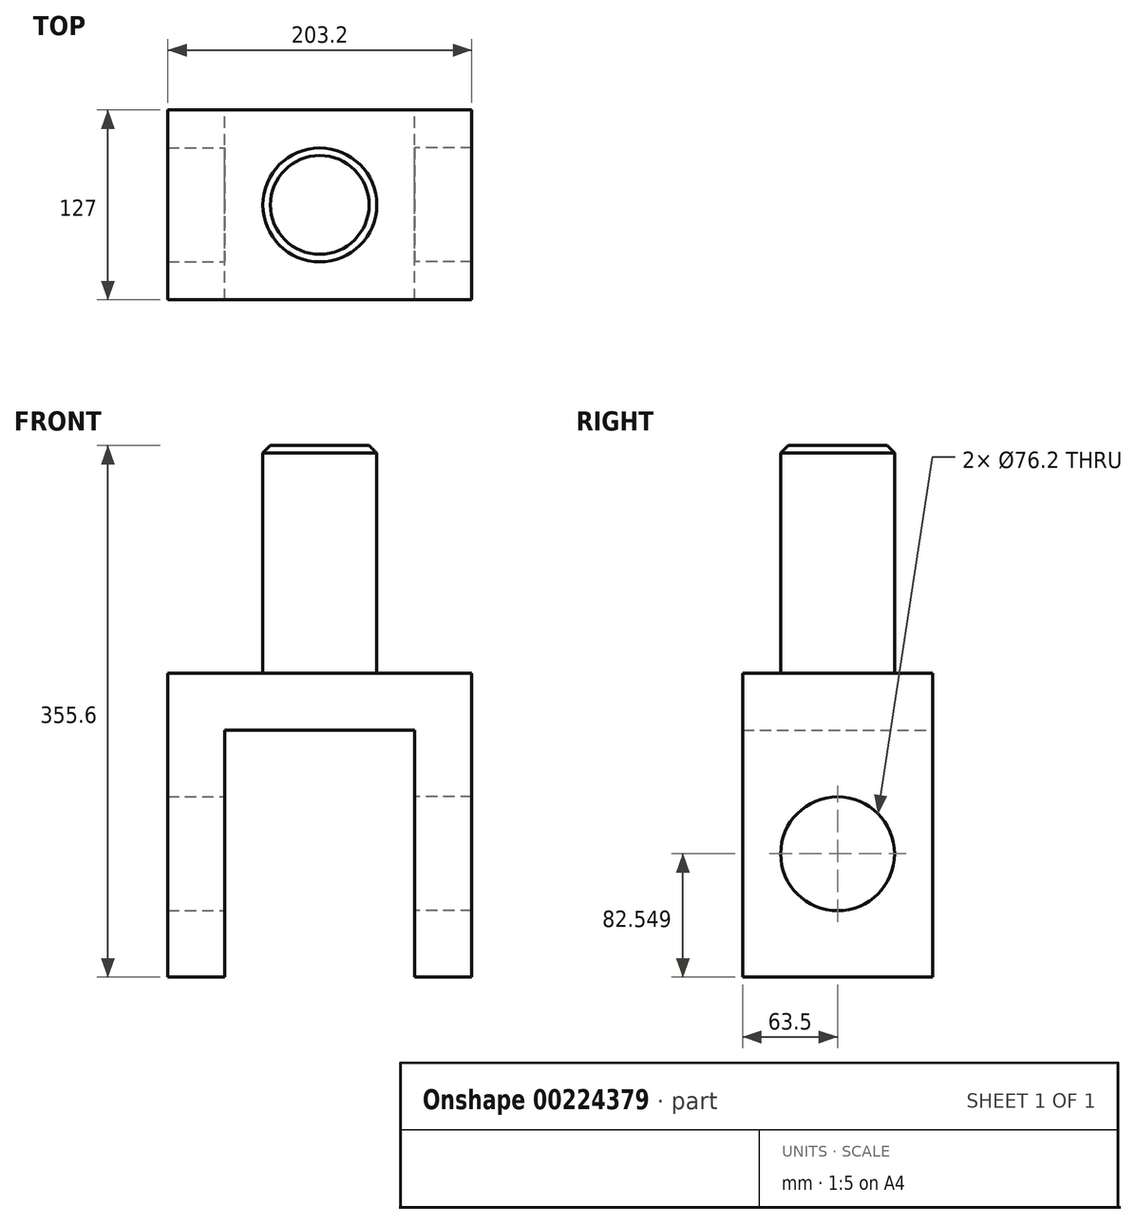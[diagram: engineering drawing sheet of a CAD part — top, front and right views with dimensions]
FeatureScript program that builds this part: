
annotation { "Feature Type Name" : "Feature", "Feature Type Description" : "" }
export const myFeature = defineFeature(function(context is Context, id is Id, definition is map)
    precondition{}
    {
        {
            var Q0;
            Q0=qCreatedBy(makeId("Front.planeOp"),FACE);
            var sketch = newSketch(context, id + "F0", { "sketchPlane" : qUnion([Q0])});
            skLineSegment(sketch, "E0.bottom", {"start": v(-27.24, 133.56) * mm, "end": v(-65.34, 133.56) * mm});
            skLineSegment(sketch, "E0.top", {"start": v(-27.24, -69.64) * mm, "end": v(-65.34, -69.64) * mm});
            skLineSegment(sketch, "E0.left", {"start": v(-27.24, 133.56) * mm, "end": v(-27.24, -69.64) * mm});
            skLineSegment(sketch, "E0.right", {"start": v(-65.34, 133.56) * mm, "end": v(-65.34, -69.64) * mm});
            skLineSegment(sketch, "E1.bottom", {"start": v(-27.24, 133.56) * mm, "end": v(36.26, 133.56) * mm});
            skLineSegment(sketch, "E1.top", {"start": v(-27.24, 95.46) * mm, "end": v(36.26, 95.46) * mm});
            skLineSegment(sketch, "E1.left", {"start": v(-27.24, 133.56) * mm, "end": v(-27.24, 95.46) * mm});
            skLineSegment(sketch, "E1.right", {"start": v(36.26, 133.56) * mm, "end": v(36.26, 95.46) * mm});
            skLineSegment(sketch, "E2.MirrorCS", {"start": v(99.76, 95.46) * mm, "end": v(36.26, 95.46) * mm});
            skLineSegment(sketch, "E3.MirrorCS", {"start": v(99.76, 133.56) * mm, "end": v(99.76, -69.64) * mm});
            skLineSegment(sketch, "E4.MirrorCS", {"start": v(137.86, 133.56) * mm, "end": v(137.86, -69.64) * mm});
            skLineSegment(sketch, "E5.MirrorCS", {"start": v(99.76, 133.56) * mm, "end": v(137.86, 133.56) * mm});
            skLineSegment(sketch, "E6.MirrorCS", {"start": v(99.76, 133.56) * mm, "end": v(36.26, 133.56) * mm});
            skLineSegment(sketch, "E7.MirrorCS", {"start": v(99.76, -69.64) * mm, "end": v(137.86, -69.64) * mm});
            skSolve(sketch);
        }
        {
            var Q0;
            Q0=makeQuery(id+"F0.imprint","IMPRINT",FACE,{"disambiguationData":[TD([[makeQuery(id+"F0.imprint","IMPRINT",EDGE,{"derivedFrom":sQuery(id+"F0.wireOp",EDGE,"E4.MirrorCS")}),-1.0]])]});
            var Q1;
            Q1=makeQuery(id+"F0.imprint","IMPRINT",FACE,{"disambiguationData":[TD([[makeQuery(id+"F0.imprint","IMPRINT",EDGE,{"derivedFrom":sQuery(id+"F0.wireOp",EDGE,"E1.right")}),1.0]])]});
            var Q2;
            Q2=makeQuery(id+"F0.imprint","IMPRINT",FACE,{"disambiguationData":[TD([[makeQuery(id+"F0.imprint","IMPRINT",EDGE,{"derivedFrom":sQuery(id+"F0.wireOp",EDGE,"E1.bottom")}),-1.0]])]});
            var Q3;
            Q3=makeQuery(id+"F0.imprint","IMPRINT",FACE,{"disambiguationData":[TD([[makeQuery(id+"F0.imprint","IMPRINT",EDGE,{"derivedFrom":sQuery(id+"F0.wireOp",EDGE,"E0.bottom")}),1.0]])]});
            extrude(context, id + "F1", {"entities" : qUnion([Q0, Q1, Q2, Q3]), "depth" : 127 * mm});
        }
        {
            var Q0;
            Q0=makeQuery(id+"F1.opExtrude","SWEPT_FACE",FACE,{"disambiguationData":[OSD([sQuery(id+"F0.wireOp",EDGE,"E0.bottom"),sQuery(id+"F0.wireOp",EDGE,"E1.bottom"),sQuery(id+"F0.wireOp",EDGE,"E5.MirrorCS"),sQuery(id+"F0.wireOp",EDGE,"E6.MirrorCS")])]});
            var sketch = newSketch(context, id + "F2", { "sketchPlane" : qUnion([Q0])});
            skCircle(sketch, "E8", {"center": v(36.26, -63.5) * mm, "radius": 119.81 * mm});
            skPoint(sketch, "E8.first.point", {"position": v(-65.34, 0) * mm});
            skPoint(sketch, "E8.second.point", {"position": v(137.86, -127) * mm});
            skPoint(sketch, "E8.third.point", {"position": v(137.86, 0) * mm});
            skCircle(sketch, "E9", {"center": v(36.26, -63.5) * mm, "radius": 38.1 * mm});
            skSolve(sketch);
        }
        {
            var Q0;
            Q0=makeQuery(id+"F2.imprint","IMPRINT",FACE,{"disambiguationData":[TD([[makeQuery(id+"F2.imprint","IMPRINT",EDGE,{"derivedFrom":sQuery(id+"F2.wireOp",EDGE,"E9")}),1.0]])]});
            extrude(context, id + "F3", {"entities" : qUnion([Q0]), "operationType" : NewBodyOperationType.ADD, "depth" : 152.4 * mm});
        }
        {
            var Q0;
            Q0=makeQuery(id+"F3.opExtrude","CAP_EDGE",EDGE,{"disambiguationData":[OSD([sQuery(id+"F2.wireOp",EDGE,"E9")])],"isStart":false});
            chamfer(context, id + "F4", {"entities" : qUnion([Q0]), "width" : 5.08 * mm, "tangentPropagation" : true});
        }
        {
            var Q0;
            Q0=makeQuery(id+"F1.opExtrude","SWEPT_FACE",FACE,{"disambiguationData":[OSD([sQuery(id+"F0.wireOp",EDGE,"E0.left")])]});
            var sketch = newSketch(context, id + "F5", { "sketchPlane" : qUnion([Q0])});
            skCircle(sketch, "E10", {"center": v(-63.5, 12.9) * mm, "radius": 104.15 * mm});
            skPoint(sketch, "E10.first.point", {"position": v(-127, -69.64) * mm});
            skPoint(sketch, "E10.second.point", {"position": v(0, -69.64) * mm});
            skPoint(sketch, "E10.third.point", {"position": v(0, 95.46) * mm});
            skSolve(sketch);
        }
        {
            var Q0;
            Q0=sQuery(id+"F5.wireOp",VERTEX,"E10.center");
            var Q1;
            Q1=makeQuery(id+"F1.opExtrude","SWEPT_BODY",BODY,{"disambiguationData":[OSD([sQuery(id+"F0.wireOp",EDGE,"E0.bottom"),sQuery(id+"F0.wireOp",EDGE,"E0.top"),sQuery(id+"F0.wireOp",EDGE,"E0.left"),sQuery(id+"F0.wireOp",EDGE,"E0.right"),sQuery(id+"F0.wireOp",EDGE,"E1.bottom"),sQuery(id+"F0.wireOp",EDGE,"E1.top"),sQuery(id+"F0.wireOp",EDGE,"E2.MirrorCS"),sQuery(id+"F0.wireOp",EDGE,"E3.MirrorCS"),sQuery(id+"F0.wireOp",EDGE,"E4.MirrorCS"),sQuery(id+"F0.wireOp",EDGE,"E5.MirrorCS"),sQuery(id+"F0.wireOp",EDGE,"E6.MirrorCS"),sQuery(id+"F0.wireOp",EDGE,"E7.MirrorCS")])]});
            hole(context, id + "F6", {"style" : HoleStyle.SIMPLE, "endStyle" : HoleEndStyle.THROUGH, "holeDiameter" : 76.2 * mm, "locations" : qUnion([Q0]), "scope" : qUnion([Q1]), "isTappedThrough" : true});
        }
        {
            var Q0;
            Q0=sQuery(id+"F5.wireOp",VERTEX,"E10.center");
            var Q1;
            Q1=makeQuery(id+"F1.opExtrude","SWEPT_BODY",BODY,{"disambiguationData":[OSD([sQuery(id+"F0.wireOp",EDGE,"E0.bottom"),sQuery(id+"F0.wireOp",EDGE,"E0.top"),sQuery(id+"F0.wireOp",EDGE,"E0.left"),sQuery(id+"F0.wireOp",EDGE,"E0.right"),sQuery(id+"F0.wireOp",EDGE,"E1.bottom"),sQuery(id+"F0.wireOp",EDGE,"E1.top"),sQuery(id+"F0.wireOp",EDGE,"E2.MirrorCS"),sQuery(id+"F0.wireOp",EDGE,"E3.MirrorCS"),sQuery(id+"F0.wireOp",EDGE,"E4.MirrorCS"),sQuery(id+"F0.wireOp",EDGE,"E5.MirrorCS"),sQuery(id+"F0.wireOp",EDGE,"E6.MirrorCS"),sQuery(id+"F0.wireOp",EDGE,"E7.MirrorCS")])]});
            hole(context, id + "F7", {"style" : HoleStyle.SIMPLE, "endStyle" : HoleEndStyle.THROUGH, "oppositeDirection" : true, "holeDiameter" : 76.2 * mm, "locations" : qUnion([Q0]), "scope" : qUnion([Q1]), "isTappedThrough" : true});
        }
    });
